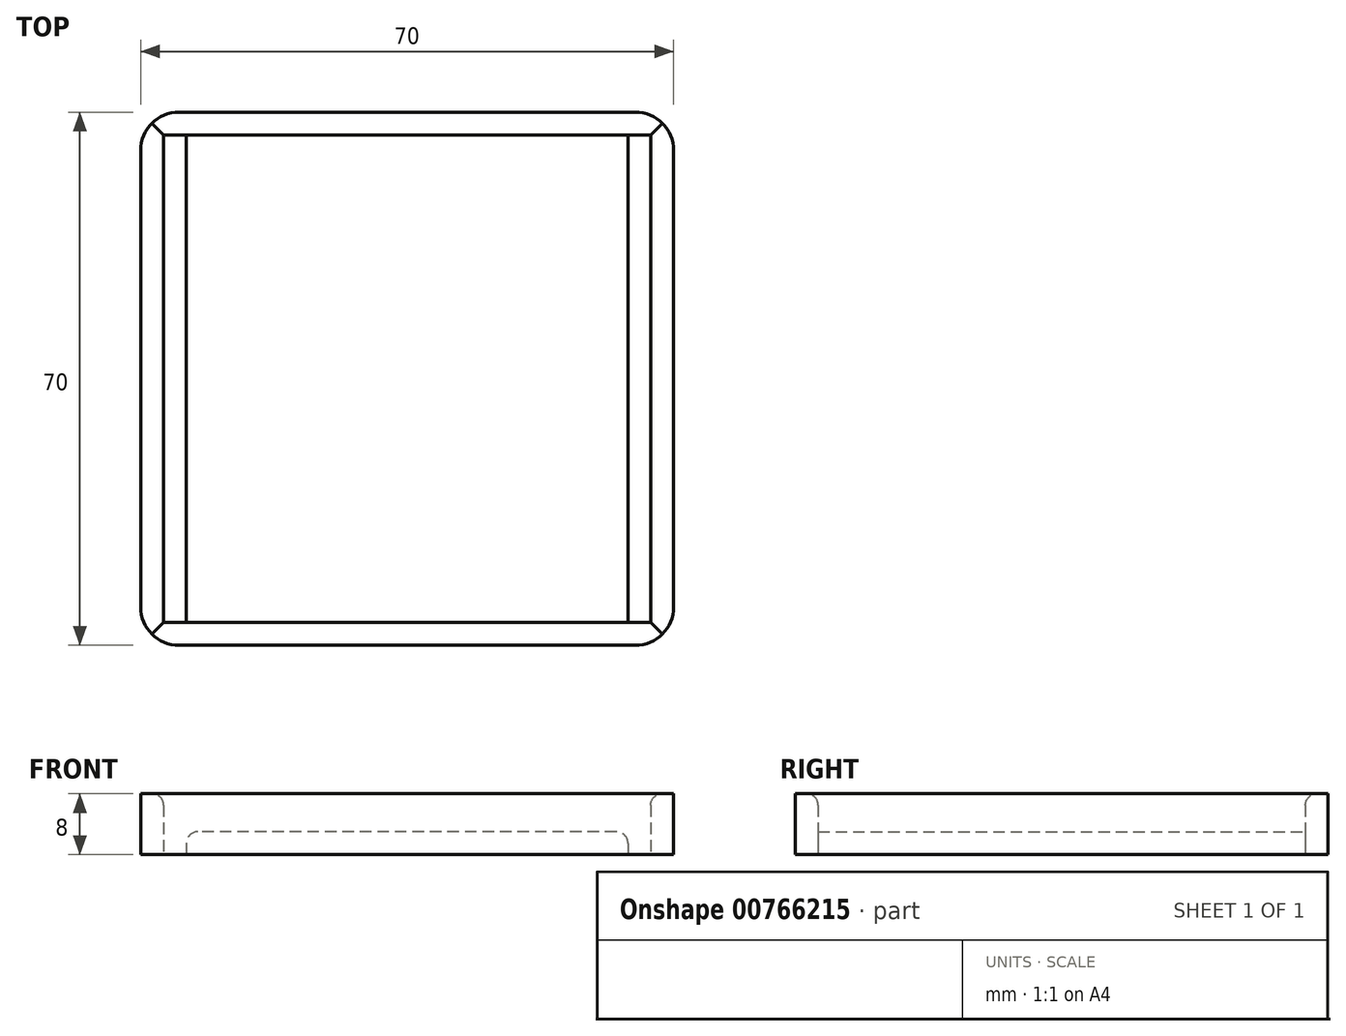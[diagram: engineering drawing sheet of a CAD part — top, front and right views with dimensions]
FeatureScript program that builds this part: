
annotation { "Feature Type Name" : "Feature", "Feature Type Description" : "" }
export const myFeature = defineFeature(function(context is Context, id is Id, definition is map)
    precondition{}
    {
        {
            var Q0;
            Q0=qCreatedBy(makeId("Top.planeOp"),FACE);
            var sketch = newSketch(context, id + "F0", { "sketchPlane" : qUnion([Q0])});
            skLineSegment(sketch, "E0.bottom", {"start": v(16, -16) * mm, "end": v(-16, -16) * mm, "construction": true});
            skLineSegment(sketch, "E0.top", {"start": v(16, 16) * mm, "end": v(-16, 16) * mm});
            skLineSegment(sketch, "E0.left", {"start": v(16, -16) * mm, "end": v(16, 16) * mm, "construction": true});
            skLineSegment(sketch, "E0.right", {"start": v(-16, -16) * mm, "end": v(-16, 16) * mm});
            skPoint(sketch, "E0.middle", {"position": v(0, 0) * mm});
            skLineSegment(sketch, "E1", {"start": v(-13, 16) * mm, "end": v(-13, -16) * mm});
            skLineSegment(sketch, "E2", {"start": v(-16, -16) * mm, "end": v(-19, -16) * mm});
            skLineSegment(sketch, "E3", {"start": v(-19, -16) * mm, "end": v(-19, 19) * mm});
            skLineSegment(sketch, "E4", {"start": v(-19, 19) * mm, "end": v(16, 19) * mm});
            skLineSegment(sketch, "E5", {"start": v(16, 19) * mm, "end": v(16, 16) * mm});
            skLineSegment(sketch, "E6.MirrorCS", {"start": v(-13, -48) * mm, "end": v(-13, -16) * mm});
            skLineSegment(sketch, "E7.MirrorCS", {"start": v(16, -48) * mm, "end": v(-16, -48) * mm});
            skLineSegment(sketch, "E8.MirrorCS", {"start": v(-19, -16) * mm, "end": v(-19, -51) * mm});
            skLineSegment(sketch, "E9.MirrorCS", {"start": v(-19, -51) * mm, "end": v(16, -51) * mm});
            skLineSegment(sketch, "E10.MirrorCS", {"start": v(-16, -16) * mm, "end": v(-16, -48) * mm});
            skLineSegment(sketch, "E11.MirrorCS", {"start": v(16, 16) * mm, "end": v(48, 16) * mm});
            skLineSegment(sketch, "E12.MirrorCS", {"start": v(51, 19) * mm, "end": v(16, 19) * mm});
            skLineSegment(sketch, "E13.MirrorCS", {"start": v(45, 16) * mm, "end": v(45, -16) * mm});
            skLineSegment(sketch, "E14.MirrorCS", {"start": v(48, -16) * mm, "end": v(48, 16) * mm});
            skLineSegment(sketch, "E15.MirrorCS", {"start": v(51, -16) * mm, "end": v(51, 19) * mm});
            skLineSegment(sketch, "E16.MirrorCS", {"start": v(45, -48) * mm, "end": v(45, -16) * mm});
            skLineSegment(sketch, "E17.MirrorCS", {"start": v(48, -16) * mm, "end": v(48, -48) * mm});
            skLineSegment(sketch, "E18.MirrorCS", {"start": v(51, -16) * mm, "end": v(51, -51) * mm});
            skLineSegment(sketch, "E19.MirrorCS", {"start": v(16, -48) * mm, "end": v(48, -48) * mm});
            skLineSegment(sketch, "E20.MirrorCS", {"start": v(51, -51) * mm, "end": v(16, -51) * mm});
            skSolve(sketch);
        }
        {
            var Q0;
            {var subQ5=sQuery(id+"F0.wireOp",EDGE,"E1");Q0=makeQuery(id+"F0.imprint","IMPRINT",FACE,{"disambiguationData":[TD([[makeQuery(id+"F0.imprint","IMPRINT",EDGE,{"derivedFrom":subQ5}),1.0]])]});}
            extrude(context, id + "F1", {"entities" : qUnion([Q0]), "depth" : 3 * mm, "offsetDistance" : 25 * mm});
        }
        {
            var Q0;
            {var subQ0=sQuery(id+"F0.wireOp",EDGE,"E0.right");Q0=makeQuery(id+"F0.imprint","IMPRINT",FACE,{"disambiguationData":[TD([[makeQuery(id+"F0.imprint","IMPRINT",EDGE,{"derivedFrom":subQ0}),1.0]])]});}
            var Q1;
            Q1=makeQuery(id+"F0.imprint","IMPRINT",FACE,{"disambiguationData":[TD([[makeQuery(id+"F0.imprint","IMPRINT",EDGE,{"derivedFrom":sQuery(id+"F0.wireOp",EDGE,"E2")}),1.0]])]});
            extrude(context, id + "F2", {"entities" : qUnion([Q0, Q1]), "operationType" : NewBodyOperationType.ADD, "depth" : 8 * mm, "offsetDistance" : 25 * mm});
        }
        {
            var Q0;
            Q0=makeQuery(id+"F2.opExtrude","SWEPT_EDGE",EDGE,{"disambiguationData":[OSD([sQuery(id+"F0.wireOp",EDGE,"E3"),sQuery(id+"F0.wireOp",EDGE,"E4")])]});
            var Q1;
            Q1=makeQuery(id+"F2.opExtrude","SWEPT_EDGE",EDGE,{"disambiguationData":[OSD([sQuery(id+"F0.wireOp",EDGE,"E8.MirrorCS"),sQuery(id+"F0.wireOp",EDGE,"E9.MirrorCS")])]});
            var Q2;
            Q2=makeQuery(id+"F2.opExtrude","SWEPT_EDGE",EDGE,{"disambiguationData":[OSD([sQuery(id+"F0.wireOp",EDGE,"E18.MirrorCS"),sQuery(id+"F0.wireOp",EDGE,"E20.MirrorCS")])]});
            var Q3;
            Q3=makeQuery(id+"F2.opExtrude","SWEPT_EDGE",EDGE,{"disambiguationData":[OSD([sQuery(id+"F0.wireOp",EDGE,"E12.MirrorCS"),sQuery(id+"F0.wireOp",EDGE,"E15.MirrorCS")])]});
            fillet(context, id + "F3", {"entities" : qUnion([Q0, Q1, Q2, Q3]), "radius" : 5 * mm, "tangentPropagation" : true, "allowEdgeOverflow" : false});
        }
        {
            var Q0;
            Q0=makeQuery(id+"F2.opExtrude","CAP_EDGE",EDGE,{"disambiguationData":[OSD([sQuery(id+"F0.wireOp",EDGE,"E0.right"),sQuery(id+"F0.wireOp",EDGE,"E10.MirrorCS")])],"isStart":false});
            var Q1;
            Q1=makeQuery(id+"F2.opExtrude","CAP_EDGE",EDGE,{"disambiguationData":[OSD([sQuery(id+"F0.wireOp",EDGE,"E0.top"),sQuery(id+"F0.wireOp",EDGE,"E11.MirrorCS")])],"isStart":false});
            var Q2;
            Q2=makeQuery(id+"F2.opExtrude","CAP_EDGE",EDGE,{"disambiguationData":[OSD([sQuery(id+"F0.wireOp",EDGE,"E14.MirrorCS"),sQuery(id+"F0.wireOp",EDGE,"E17.MirrorCS")])],"isStart":false});
            var Q3;
            Q3=makeQuery(id+"F2.opExtrude","CAP_EDGE",EDGE,{"disambiguationData":[OSD([sQuery(id+"F0.wireOp",EDGE,"E7.MirrorCS"),sQuery(id+"F0.wireOp",EDGE,"E19.MirrorCS")])],"isStart":false});
            var Q4;
            Q4=makeQuery(id+"F1.opExtrude","CAP_EDGE",EDGE,{"disambiguationData":[OSD([sQuery(id+"F0.wireOp",EDGE,"E1"),sQuery(id+"F0.wireOp",EDGE,"E6.MirrorCS")])],"isStart":false});
            var Q5;
            Q5=makeQuery(id+"F1.opExtrude","CAP_EDGE",EDGE,{"disambiguationData":[OSD([sQuery(id+"F0.wireOp",EDGE,"E13.MirrorCS"),sQuery(id+"F0.wireOp",EDGE,"E16.MirrorCS")])],"isStart":false});
            fillet(context, id + "F4", {"entities" : qUnion([Q0, Q1, Q2, Q3, Q4, Q5]), "radius" : 1.5 * mm, "tangentPropagation" : true, "allowEdgeOverflow" : false});
        }
    });
